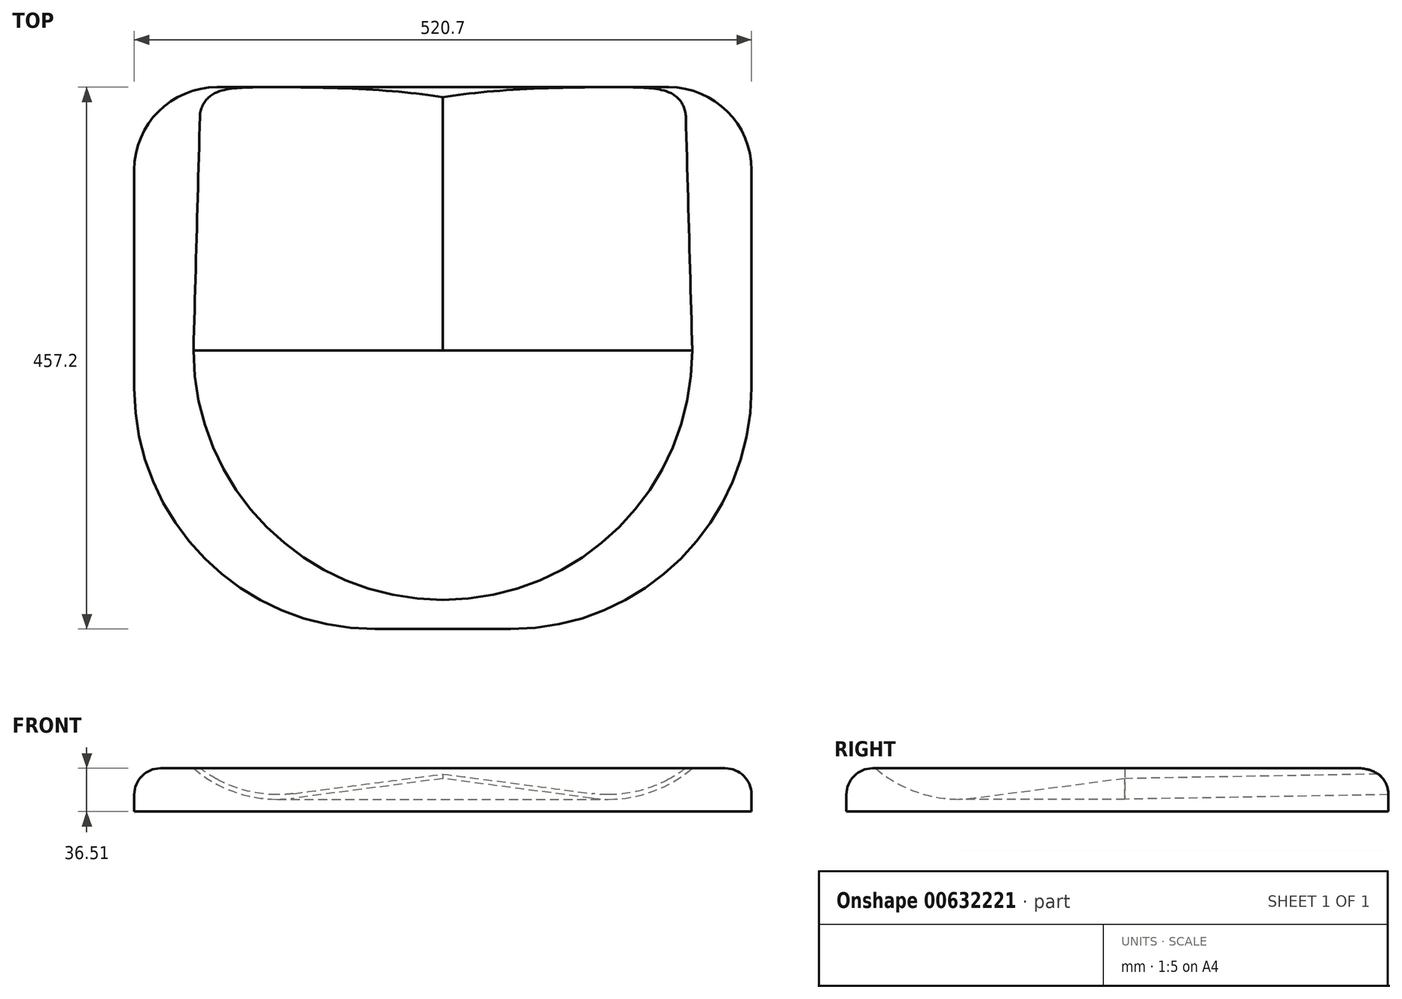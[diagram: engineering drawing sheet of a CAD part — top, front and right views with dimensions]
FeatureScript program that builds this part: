
annotation { "Feature Type Name" : "Feature", "Feature Type Description" : "" }
export const myFeature = defineFeature(function(context is Context, id is Id, definition is map)
    precondition{}
    {
        {
            var Q0;
            Q0=qCreatedBy(makeId("Top.planeOp"),FACE);
            var sketch = newSketch(context, id + "F0", { "sketchPlane" : qUnion([Q0])});
            skLineSegment(sketch, "E0.bottom", {"start": v(260.35, 228.6) * mm, "end": v(-260.35, 228.6) * mm});
            skLineSegment(sketch, "E0.top", {"start": v(260.35, -228.6) * mm, "end": v(-260.35, -228.6) * mm});
            skLineSegment(sketch, "E0.left", {"start": v(260.35, 228.6) * mm, "end": v(260.35, -228.6) * mm});
            skLineSegment(sketch, "E0.right", {"start": v(-260.35, 228.6) * mm, "end": v(-260.35, -228.6) * mm});
            skPoint(sketch, "E0.middle", {"position": v(0, 0) * mm});
            skSolve(sketch);
        }
        {
            var Q0;
            Q0 = qSketchRegion(id + "F0", true);
            extrude(context, id + "F1", {"entities" : qUnion([Q0]), "depth" : 36.5 * mm, "offsetDistance" : 25.4 * mm});
        }
        {
            var Q0;
            Q0=makeQuery(id+"F1.opExtrude","SWEPT_EDGE",EDGE,{"disambiguationData":[OSD([sQuery(id+"F0.wireOp",EDGE,"E0.top"),sQuery(id+"F0.wireOp",EDGE,"E0.right")])]});
            var Q1;
            Q1=makeQuery(id+"F1.opExtrude","SWEPT_EDGE",EDGE,{"disambiguationData":[OSD([sQuery(id+"F0.wireOp",EDGE,"E0.top"),sQuery(id+"F0.wireOp",EDGE,"E0.left")])]});
            fillet(context, id + "F2", {"entities" : qUnion([Q0, Q1]), "radius" : 203.2 * mm, "tangentPropagation" : true, "allowEdgeOverflow" : false});
        }
        {
            var Q0;
            Q0=makeQuery(id+"F1.opExtrude","SWEPT_EDGE",EDGE,{"disambiguationData":[OSD([sQuery(id+"F0.wireOp",EDGE,"E0.bottom"),sQuery(id+"F0.wireOp",EDGE,"E0.left")])]});
            var Q1;
            Q1=makeQuery(id+"F1.opExtrude","SWEPT_EDGE",EDGE,{"disambiguationData":[OSD([sQuery(id+"F0.wireOp",EDGE,"E0.bottom"),sQuery(id+"F0.wireOp",EDGE,"E0.right")])]});
            fillet(context, id + "F3", {"entities" : qUnion([Q0, Q1]), "radius" : 69.85 * mm, "tangentPropagation" : true, "allowEdgeOverflow" : false});
        }
        {
            var Q0;
            Q0=makeQuery(id+"F1.opExtrude","CAP_EDGE",EDGE,{"disambiguationData":[OSD([sQuery(id+"F0.wireOp",EDGE,"E0.bottom")])],"isStart":false});
            fillet(context, id + "F4", {"entities" : qUnion([Q0]), "radius" : 22.22 * mm, "tangentPropagation" : true, "allowEdgeOverflow" : false});
        }
        {
            var Q0;
            Q0=makeQuery(id+"F1.opExtrude","SWEPT_FACE",FACE,{"disambiguationData":[OSD([sQuery(id+"F0.wireOp",EDGE,"E0.bottom")])]});
            var sketch = newSketch(context, id + "F5", { "sketchPlane" : qUnion([Q0])});
            skLineSegment(sketch, "E1.0", {"start": v(-190.5, 0) * mm, "end": v(190.5, 0) * mm, "construction": true});
            skLineSegment(sketch, "E2.0", {"start": v(-190.5, 36.51) * mm, "end": v(190.5, 36.51) * mm, "construction": true});
            skArc(sketch, "E3", {"start": v(-105.15, 217.98) * mm, "mid": v(-243.92, 129.79) * mm, "end": v(-126.02, 15.18) * mm});
            skPoint(sketch, "E4.middle", {"position": v(41.89, 93.41) * mm});
            skLineSegment(sketch, "E5", {"start": v(0, 181.25) * mm, "end": v(-105.15, 217.98) * mm});
            skLineSegment(sketch, "E6", {"start": v(0, 31.78) * mm, "end": v(-126.02, 15.18) * mm});
            skPoint(sketch, "E4.top.start.orphan", {"position": v(-46.76, 137.86) * mm});
            skPoint(sketch, "E7.orphan", {"position": v(32.98, 23.31) * mm});
            skLineSegment(sketch, "E8", {"start": v(0, 36.51) * mm, "end": v(0, 317.86) * mm, "construction": true});
            skLineSegment(sketch, "E9.MirrorCS", {"start": v(0, 181.25) * mm, "end": v(105.15, 217.98) * mm});
            skLineSegment(sketch, "E10.MirrorCS", {"start": v(0, 31.78) * mm, "end": v(126.02, 15.18) * mm});
            skArc(sketch, "E11.MirrorCS", {"start": v(105.15, 217.98) * mm, "mid": v(243.92, 129.79) * mm, "end": v(126.02, 15.18) * mm});
            skPoint(sketch, "E12.orphan", {"position": v(-50.8, 163.51) * mm});
            skPoint(sketch, "E4.right.end.orphan", {"position": v(50.8, 163.51) * mm});
            skPoint(sketch, "E13.MirrorCS.start.orphan", {"position": v(-130.54, 48.96) * mm});
            skPoint(sketch, "E14.orphan", {"position": v(130.54, 48.96) * mm});
            skLineSegment(sketch, "E15", {"start": v(-139.7, 119.06) * mm, "end": v(139.7, 119.06) * mm, "construction": true});
            skSolve(sketch);
        }
        {
            var Q0;
            Q0 = qSketchRegion(id + "F5", true);
            extrude(context, id + "F6", {"entities" : qUnion([Q0]), "operationType" : NewBodyOperationType.REMOVE, "oppositeDirection" : true, "depth" : 222.25 * mm, "offsetDistance" : 25.4 * mm, "hasDraft" : true, "draftAngle" : 1 * degree});
        }
        {
            var Q0;
            {var subQ0=sQuery(id+"F5.wireOp",EDGE,"E3");var subQ1=sQuery(id+"F5.wireOp",EDGE,"E6");Q0=makeQuery(id+"F6.boolean.opBoolean","COPY",FACE,{"disambiguationData":[TD([makeQuery(id+"F6.opExtrude","SWEPT_FACE",FACE,{"disambiguationData":[OSD([subQ0])]})])],"derivedFrom":makeQuery(id+"F6.opExtrude","CAP_FACE",FACE,{"disambiguationData":[OSD([subQ0,sQuery(id+"F5.wireOp",EDGE,"E5"),subQ1,sQuery(id+"F5.wireOp",EDGE,"E9.MirrorCS"),sQuery(id+"F5.wireOp",EDGE,"E10.MirrorCS"),sQuery(id+"F5.wireOp",EDGE,"E11.MirrorCS")])],"isStart":false})});}
            var sketch = newSketch(context, id + "F7", { "sketchPlane" : qUnion([Q0])});
            skLineSegment(sketch, "E16.0", {"start": v(-210.35, 36.51) * mm, "end": v(0, 36.51) * mm});
            skArc(sketch, "E17.0", {"start": v(-210.35, 36.51) * mm, "mid": v(-170.61, 14.9) * mm, "end": v(-125.52, 11.34) * mm});
            skLineSegment(sketch, "E18.0", {"start": v(0, 27.86) * mm, "end": v(-125.52, 11.34) * mm});
            skLineSegment(sketch, "E19", {"start": v(0, 27.86) * mm, "end": v(0, 36.51) * mm});
            skPoint(sketch, "E20.orphan", {"position": v(210.35, 36.51) * mm});
            skSolve(sketch);
        }
        {
            var Q0;
            Q0=makeQuery(id+"F7.imprint","IMPRINT",FACE,{"disambiguationData":[TD([[makeQuery(id+"F7.imprint","IMPRINT",EDGE,{"derivedFrom":sQuery(id+"F7.wireOp",EDGE,"b9f270c6-e9c4-43ee-826b-f588c1038c94.0.0")}),1.0]])]});
            var Q1;
            Q1=makeQuery(id+"F7.imprint","IMPRINT",FACE,{"disambiguationData":[TD([[makeQuery(id+"F7.imprint","IMPRINT",EDGE,{"derivedFrom":sQuery(id+"F7.wireOp",EDGE,"E16.0")}),-1.0]])]});
            var Q2;
            Q2=sQuery(id+"F7.wireOp",EDGE,"b9f270c6-e9c4-43ee-826b-f588c1038c94.0.2");
            var Q3;
            Q3=sQuery(id+"F7.wireOp",EDGE,"b9f270c6-e9c4-43ee-826b-f588c1038c94.0.0");
            var Q4;
            Q4=sQuery(id+"F7.wireOp",EDGE,"b9f270c6-e9c4-43ee-826b-f588c1038c94.0.1");
            var Q5;
            Q5=sQuery(id+"F7.wireOp",EDGE,"E19");
            revolve(context, id + "F8", {"operationType" : NewBodyOperationType.REMOVE, "entities" : qUnion([Q0, Q1]), "surfaceEntities" : qUnion([Q2, Q3, Q4]), "axis" : qUnion([Q5]), "revolveType" : RevolveType.ONE_DIRECTION, "oppositeDirection" : true, "angle" : 180 * degree});
        }
    });
